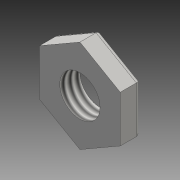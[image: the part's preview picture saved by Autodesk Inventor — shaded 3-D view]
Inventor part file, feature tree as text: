
AUTODESK INVENTOR PART (.ipt)
format: ipt  version: 2016 (Build 200138000, 138)  size: 93,184 bytes
history: native  units: mm
features: extrude x1, fillet x1, thread x1, sketch x1
ambient origin geometry x8: Origin, YZ Plane, XZ Plane, XY Plane, X Axis, Y Axis, Z Axis, Center Point
bodies: 实体1 (feature_tree)
feature tree (4):
  extrude  "拉伸1"  Depth=2.0mm TaperAngle=0.0deg
  fillet  "圆角1"  Radius=0.4mm
  thread  "螺纹1"  [1 undecoded]
  sketch  "草图1"  dims[d0=4.0mm d2=2.0mm d3=0.0mm d4=0.4mm d5=10.0mm d6=0.0mm]
note: 1 required parameter value undecoded (feature->parameter linkage not recoverable at this tier; creation-order binding heuristic only, values carry confidence <= 0.55)
